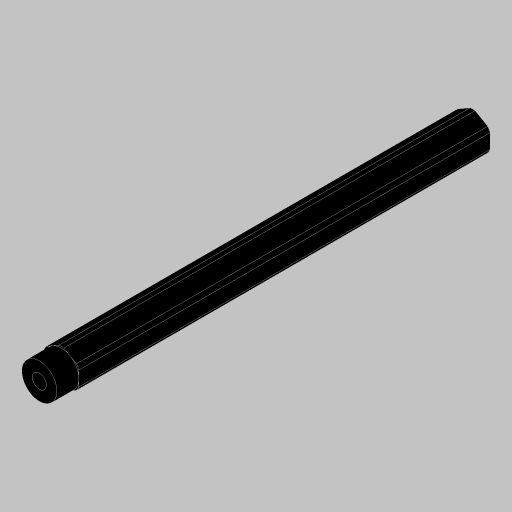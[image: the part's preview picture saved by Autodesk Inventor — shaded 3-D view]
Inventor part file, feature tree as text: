
AUTODESK INVENTOR PART (.ipt)
format: ipt  version: 2023.5 (Build 275446000, 446)  size: 144,896 bytes
history: native  units: in
note: dims shown in document units (in); Inventor stores cm internally (conversion verified against a paired STEP export)
features: extrude x3, projected_geometry x3, hole x1, sketch x1
ambient origin geometry x8: Origin, YZ Plane, XZ Plane, XY Plane, X Axis, Y Axis, Z Axis, Center Point
bodies: Solid1 (feature_tree)
feature tree (8):
  extrude  "Extrusion1"  Depth=0.315in
  hole  "Hole1"  [1 undecoded]
  extrude  "Extrusion3"  Depth=0.5in
  extrude  "Extrusion4"  Depth=0.315in TaperAngle=0.0deg
  sketch  "Sketch5"  dims[d2=0.0in d9=0.625in d10=0.385in d11=0.25in d12=0.5635in d13=1.0in d14=0.8108in d16=0.7in d17=0.0in d18=0.0in d19=0.5in d20=0.315in d21=0.0in]
  projected_geometry  "Projected Loop2"
  projected_geometry  "Project Cut Edges1"
  projected_geometry  "Project Cut Edges2"
note: 1 required parameter value undecoded (feature->parameter linkage not recoverable at this tier; creation-order binding heuristic only, values carry confidence <= 0.55)
